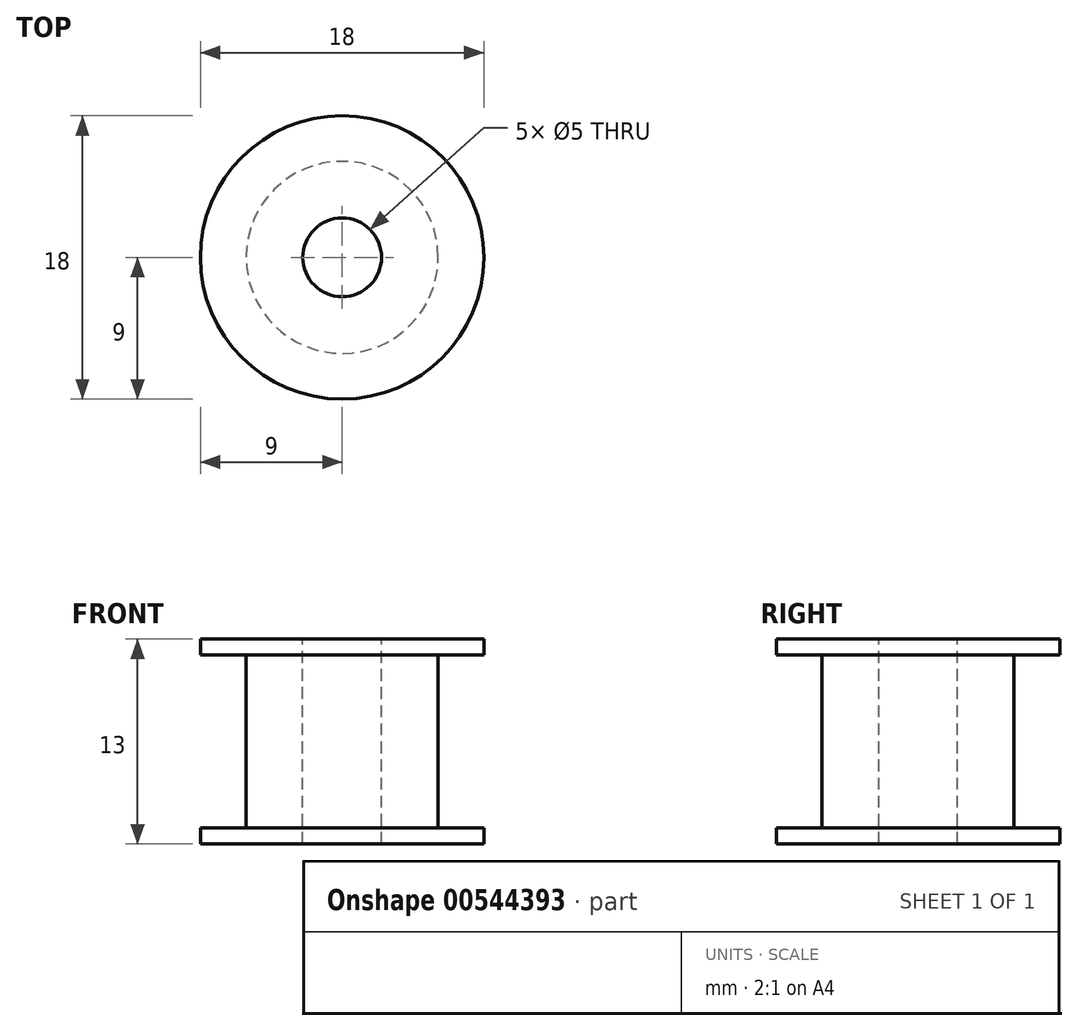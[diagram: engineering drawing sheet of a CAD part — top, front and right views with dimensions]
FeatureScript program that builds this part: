
annotation { "Feature Type Name" : "Feature", "Feature Type Description" : "" }
export const myFeature = defineFeature(function(context is Context, id is Id, definition is map)
    precondition{}
    {
        {
            var Q0;
            Q0=qCreatedBy(makeId("Front.planeOp"),FACE);
            var sketch = newSketch(context, id + "F0", { "sketchPlane" : qUnion([Q0])});
            skLineSegment(sketch, "E0", {"start": v(0, 7.5) * mm, "end": v(0, -7.63) * mm, "construction": true});
            skLineSegment(sketch, "E1", {"start": v(2.5, 6.5) * mm, "end": v(9, 6.5) * mm});
            skLineSegment(sketch, "E2", {"start": v(9, 6.5) * mm, "end": v(9, 5.5) * mm});
            skLineSegment(sketch, "E3", {"start": v(9, 5.5) * mm, "end": v(6.1, 5.5) * mm});
            skLineSegment(sketch, "E4", {"start": v(6.1, 5.5) * mm, "end": v(6.1, -5.5) * mm});
            skLineSegment(sketch, "E5", {"start": v(6.1, -5.5) * mm, "end": v(9, -5.5) * mm});
            skLineSegment(sketch, "E6", {"start": v(9, -5.5) * mm, "end": v(9, -6.5) * mm});
            skLineSegment(sketch, "E7", {"start": v(9, -6.5) * mm, "end": v(2.5, -6.5) * mm});
            skLineSegment(sketch, "E8", {"start": v(-6.47, 0) * mm, "end": v(20.28, 0) * mm, "construction": true});
            skLineSegment(sketch, "E9", {"start": v(2.5, 6.5) * mm, "end": v(2.5, -6.5) * mm});
            skSolve(sketch);
        }
        {
            var Q0;
            Q0=qSketchRegion(id+"F0",true);
            var Q1;
            Q1=sQuery(id+"F0.wireOp",EDGE,"E0");
            revolve(context, id + "F1", {"entities" : qUnion([Q0]), "axis" : qUnion([Q1]), "revolveType" : RevolveType.FULL});
        }
    });
